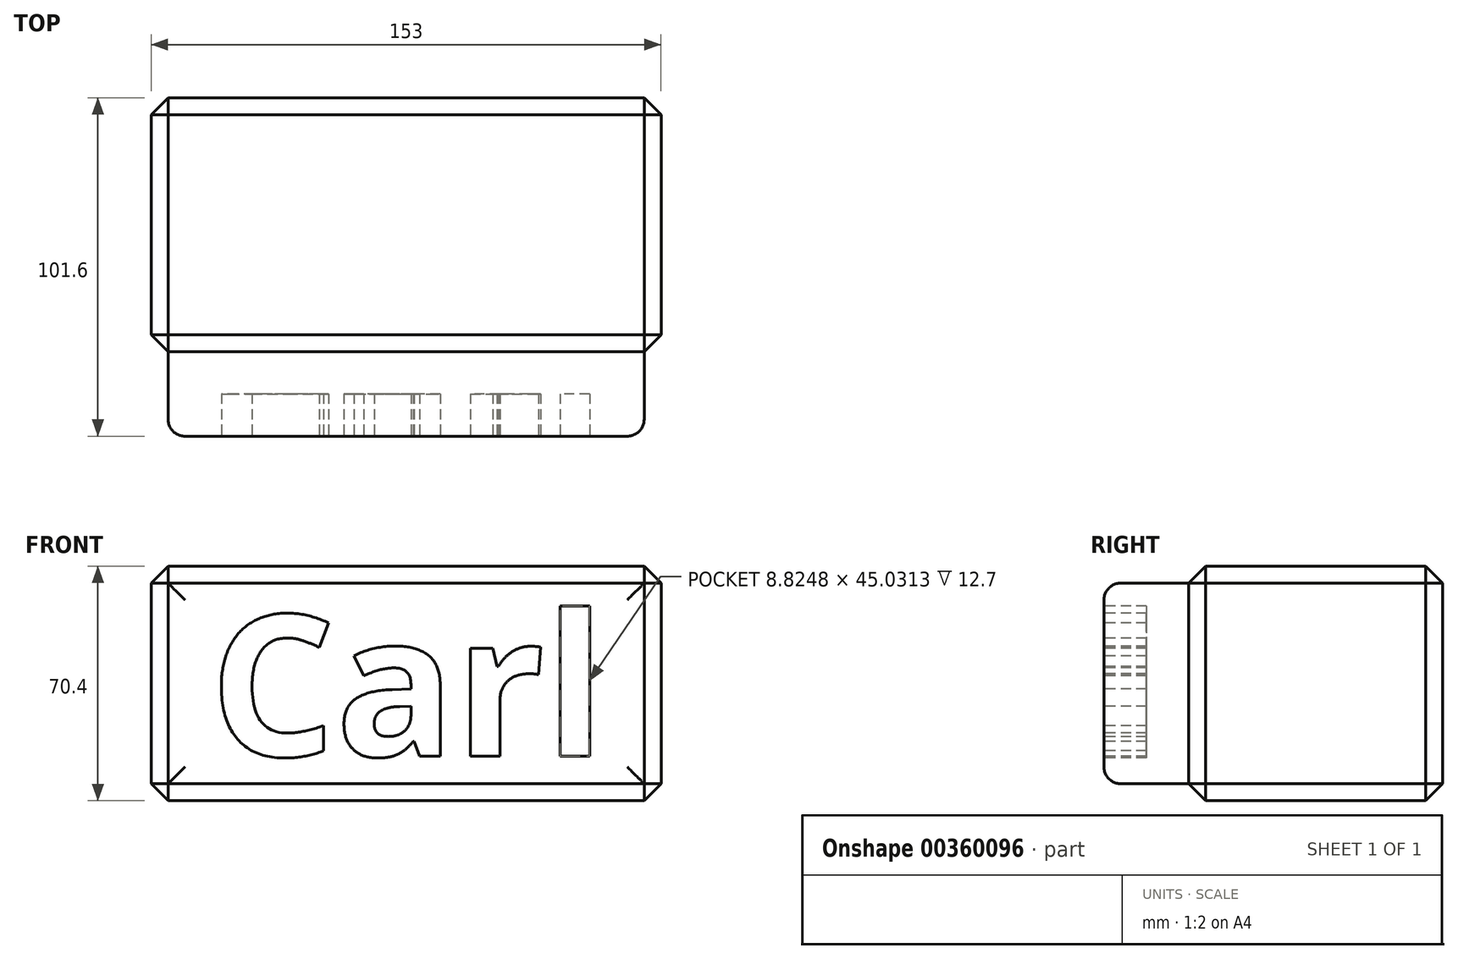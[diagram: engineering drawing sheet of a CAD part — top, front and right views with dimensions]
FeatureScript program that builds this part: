
annotation { "Feature Type Name" : "Feature", "Feature Type Description" : "" }
export const myFeature = defineFeature(function(context is Context, id is Id, definition is map)
    precondition{}
    {
        {
            var Q0;
            Q0=qCreatedBy(makeId("Front.planeOp"),FACE);
            var sketch = newSketch(context, id + "F0", { "sketchPlane" : qUnion([Q0])});
            skLineSegment(sketch, "E0.bottom", {"start": v(-76.5, 35.2) * mm, "end": v(76.5, 35.2) * mm});
            skLineSegment(sketch, "E0.top", {"start": v(-76.5, -35.2) * mm, "end": v(76.5, -35.2) * mm});
            skLineSegment(sketch, "E0.left", {"start": v(-76.5, 35.2) * mm, "end": v(-76.5, -35.2) * mm});
            skLineSegment(sketch, "E0.right", {"start": v(76.5, 35.2) * mm, "end": v(76.5, -35.2) * mm});
            skPoint(sketch, "E0.middle", {"position": v(0, 0) * mm});
            skSolve(sketch);
        }
        {
            var Q0;
            Q0 = qSketchRegion(id + "F0", true);
            extrude(context, id + "F1", {"entities" : qUnion([Q0]), "depth" : 76.2 * mm});
        }
        {
            var Q0;
            Q0=makeQuery(id+"F1.opExtrude","SWEPT_EDGE",EDGE,{"disambiguationData":[OSD([sQuery(id+"F0.wireOp",EDGE,"E0.bottom"),sQuery(id+"F0.wireOp",EDGE,"E0.left")])]});
            var Q1;
            Q1=makeQuery(id+"F1.opExtrude","SWEPT_FACE",FACE,{"disambiguationData":[OSD([sQuery(id+"F0.wireOp",EDGE,"E0.left")])]});
            var Q2;
            Q2=makeQuery(id+"F1.opExtrude","CAP_FACE",FACE,{"disambiguationData":[OSD([sQuery(id+"F0.wireOp",EDGE,"E0.bottom"),sQuery(id+"F0.wireOp",EDGE,"E0.top"),sQuery(id+"F0.wireOp",EDGE,"E0.left"),sQuery(id+"F0.wireOp",EDGE,"E0.right")])],"isStart":false});
            var Q3;
            Q3=makeQuery(id+"F1.opExtrude","SWEPT_FACE",FACE,{"disambiguationData":[OSD([sQuery(id+"F0.wireOp",EDGE,"E0.right")])]});
            var Q4;
            Q4=makeQuery(id+"F1.opExtrude","CAP_FACE",FACE,{"disambiguationData":[OSD([sQuery(id+"F0.wireOp",EDGE,"E0.bottom"),sQuery(id+"F0.wireOp",EDGE,"E0.top"),sQuery(id+"F0.wireOp",EDGE,"E0.left"),sQuery(id+"F0.wireOp",EDGE,"E0.right")])],"isStart":true});
            chamfer(context, id + "F2", {"entities" : qUnion([Q0, Q1, Q2, Q3, Q4]), "width" : 5.08 * mm, "tangentPropagation" : true});
        }
        {
            var Q0;
            Q0=makeQuery(id+"F1.opExtrude","CAP_FACE",FACE,{"disambiguationData":[OSD([sQuery(id+"F0.wireOp",EDGE,"E0.bottom"),sQuery(id+"F0.wireOp",EDGE,"E0.top"),sQuery(id+"F0.wireOp",EDGE,"E0.left"),sQuery(id+"F0.wireOp",EDGE,"E0.right")])],"isStart":false});
            extrude(context, id + "F3", {"entities" : qUnion([Q0]), "operationType" : NewBodyOperationType.ADD, "depth" : 25.4 * mm});
        }
        {
            var Q0;
            {var subQ0=sQuery(id+"F0.wireOp",EDGE,"E0.right");var subQ1=sQuery(id+"F0.wireOp",EDGE,"E0.left");var subQ2=sQuery(id+"F0.wireOp",EDGE,"E0.top");var subQ3=sQuery(id+"F0.wireOp",EDGE,"E0.bottom");Q0=makeQuery(id+"F3.opExtrude","CAP_EDGE",EDGE,{"disambiguationData":[OSD([subQ3,subQ2,subQ1,subQ0]),TDD([makeQuery(id+"F2.opChamfer","BLEND_EDGE",EDGE,{"blendedFrom":[makeQuery(id+"F1.opExtrude","CAP_EDGE",EDGE,{"disambiguationData":[OSD([subQ0])],"isStart":false}),makeQuery(id+"F1.opExtrude","CAP_FACE",FACE,{"disambiguationData":[OSD([subQ3,subQ2,subQ1,subQ0])],"isStart":false})],"blendedInto":[makeQuery(id+"F1.opExtrude","CAP_FACE",FACE,{"disambiguationData":[OSD([subQ3,subQ2,subQ1,subQ0])],"isStart":false})]})])],"isStart":false});}
            var Q1;
            {var subQ0=sQuery(id+"F0.wireOp",EDGE,"E0.right");var subQ1=sQuery(id+"F0.wireOp",EDGE,"E0.left");var subQ2=sQuery(id+"F0.wireOp",EDGE,"E0.top");var subQ3=sQuery(id+"F0.wireOp",EDGE,"E0.bottom");Q1=makeQuery(id+"F3.opExtrude","CAP_EDGE",EDGE,{"disambiguationData":[OSD([subQ3,subQ2,subQ1,subQ0]),TDD([makeQuery(id+"F2.opChamfer","BLEND_EDGE",EDGE,{"blendedFrom":[makeQuery(id+"F1.opExtrude","CAP_EDGE",EDGE,{"disambiguationData":[OSD([subQ3])],"isStart":false}),makeQuery(id+"F1.opExtrude","CAP_FACE",FACE,{"disambiguationData":[OSD([subQ3,subQ2,subQ1,subQ0])],"isStart":false})],"blendedInto":[makeQuery(id+"F1.opExtrude","CAP_FACE",FACE,{"disambiguationData":[OSD([subQ3,subQ2,subQ1,subQ0])],"isStart":false})]})])],"isStart":false});}
            var Q2;
            {var subQ0=sQuery(id+"F0.wireOp",EDGE,"E0.right");var subQ1=sQuery(id+"F0.wireOp",EDGE,"E0.left");var subQ2=sQuery(id+"F0.wireOp",EDGE,"E0.top");var subQ3=sQuery(id+"F0.wireOp",EDGE,"E0.bottom");Q2=makeQuery(id+"F3.opExtrude","CAP_EDGE",EDGE,{"disambiguationData":[OSD([subQ3,subQ2,subQ1,subQ0]),TDD([makeQuery(id+"F2.opChamfer","BLEND_EDGE",EDGE,{"blendedFrom":[makeQuery(id+"F1.opExtrude","CAP_EDGE",EDGE,{"disambiguationData":[OSD([subQ1])],"isStart":false}),makeQuery(id+"F1.opExtrude","CAP_FACE",FACE,{"disambiguationData":[OSD([subQ3,subQ2,subQ1,subQ0])],"isStart":false})],"blendedInto":[makeQuery(id+"F1.opExtrude","CAP_FACE",FACE,{"disambiguationData":[OSD([subQ3,subQ2,subQ1,subQ0])],"isStart":false})]})])],"isStart":false});}
            var Q3;
            {var subQ0=sQuery(id+"F0.wireOp",EDGE,"E0.right");var subQ1=sQuery(id+"F0.wireOp",EDGE,"E0.left");var subQ2=sQuery(id+"F0.wireOp",EDGE,"E0.top");var subQ3=sQuery(id+"F0.wireOp",EDGE,"E0.bottom");Q3=makeQuery(id+"F3.opExtrude","CAP_EDGE",EDGE,{"disambiguationData":[OSD([subQ3,subQ2,subQ1,subQ0]),TDD([makeQuery(id+"F2.opChamfer","BLEND_EDGE",EDGE,{"blendedFrom":[makeQuery(id+"F1.opExtrude","CAP_EDGE",EDGE,{"disambiguationData":[OSD([subQ2])],"isStart":false}),makeQuery(id+"F1.opExtrude","CAP_FACE",FACE,{"disambiguationData":[OSD([subQ3,subQ2,subQ1,subQ0])],"isStart":false})],"blendedInto":[makeQuery(id+"F1.opExtrude","CAP_FACE",FACE,{"disambiguationData":[OSD([subQ3,subQ2,subQ1,subQ0])],"isStart":false})]})])],"isStart":false});}
            fillet(context, id + "F4", {"entities" : qUnion([Q0, Q1, Q2, Q3]), "radius" : 5.08 * mm, "tangentPropagation" : true, "allowEdgeOverflow" : false});
        }
        {
            var Q0;
            Q0=makeQuery(id+"F3.opExtrude","CAP_FACE",FACE,{"disambiguationData":[OSD([sQuery(id+"F0.wireOp",EDGE,"E0.bottom"),sQuery(id+"F0.wireOp",EDGE,"E0.top"),sQuery(id+"F0.wireOp",EDGE,"E0.left"),sQuery(id+"F0.wireOp",EDGE,"E0.right")])],"isStart":false});
            var sketch = newSketch(context, id + "F5", { "sketchPlane" : qUnion([Q0])});
            skText(sketch, "E1", { "text": "Carl", "fontName": "OpenSans-Bold.ttf"});
            const initialGuessF5  = {"E1": [-0.05888, -0.0218, 1, 0, 0.04267]};
            skSetInitialGuess(sketch, initialGuessF5);
            skSolve(sketch);
        }
        {
            var Q0;
            Q0 = qSketchRegion(id + "F5", true);
            extrude(context, id + "F6", {"entities" : qUnion([Q0]), "operationType" : NewBodyOperationType.REMOVE, "oppositeDirection" : true, "depth" : 12.7 * mm});
        }
    });
